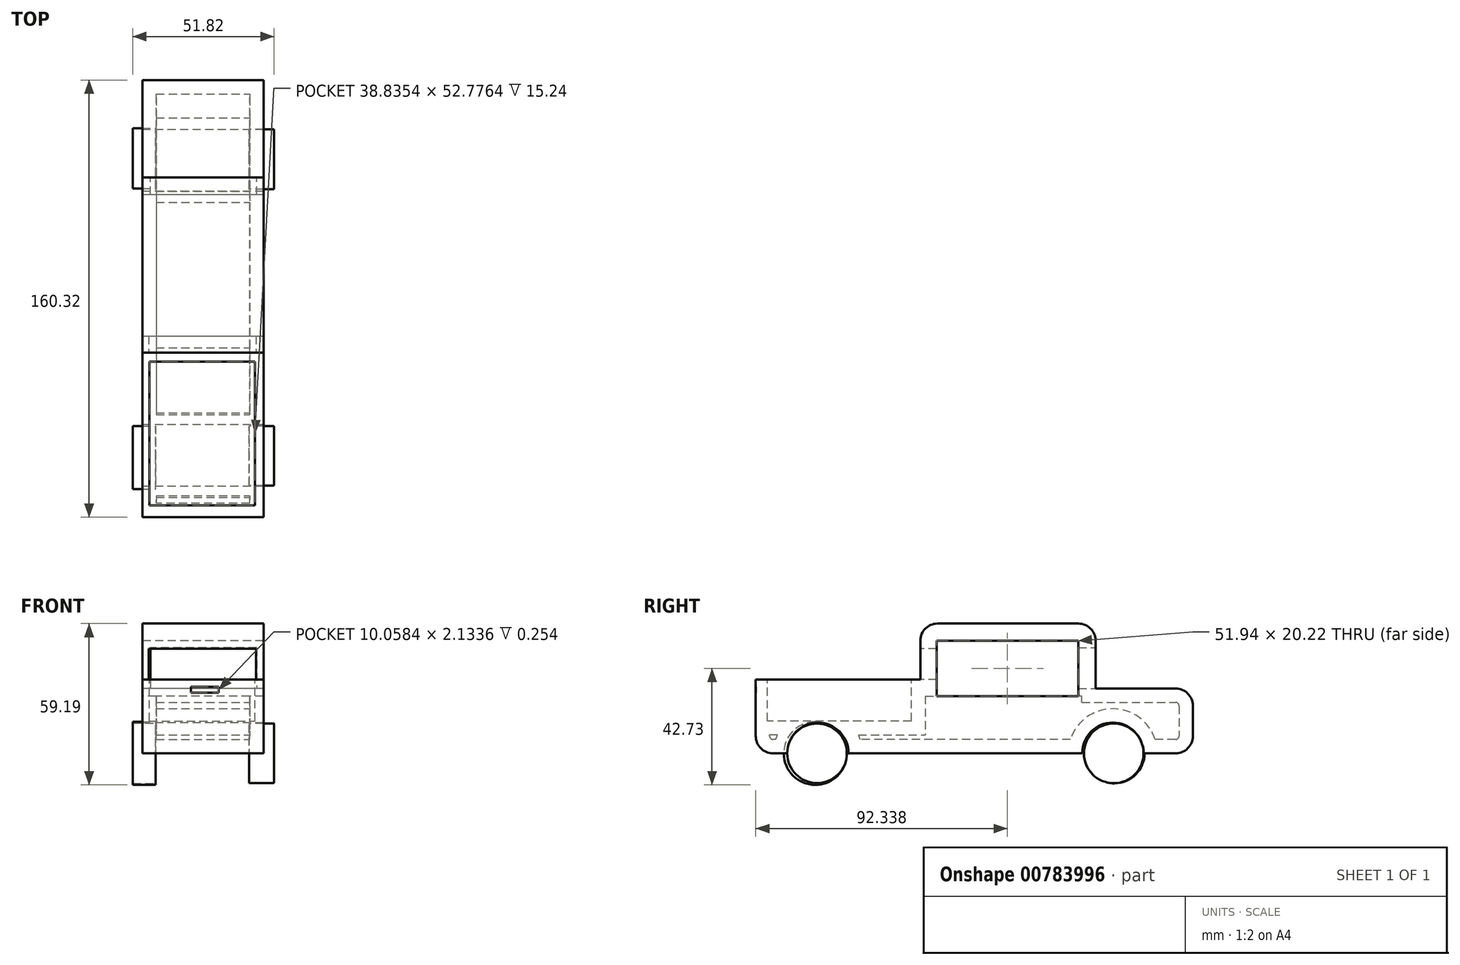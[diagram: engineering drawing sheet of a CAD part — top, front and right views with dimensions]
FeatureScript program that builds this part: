
annotation { "Feature Type Name" : "Feature", "Feature Type Description" : "" }
export const myFeature = defineFeature(function(context is Context, id is Id, definition is map)
    precondition{}
    {
        {
            var Q0;
            Q0=qCreatedBy(makeId("Right.planeOp"),FACE);
            var sketch = newSketch(context, id + "F0", { "sketchPlane" : qUnion([Q0])});
            skLineSegment(sketch, "E0.bottom", {"start": v(34.9, 23.77) * mm, "end": v(64.21, 23.77) * mm});
            skLineSegment(sketch, "E0.top", {"start": v(34.9, 0) * mm, "end": v(64.21, 0) * mm});
            skLineSegment(sketch, "E0.left", {"start": v(34.9, 23.77) * mm, "end": v(34.9, 0) * mm});
            skLineSegment(sketch, "E0.right", {"start": v(70.56, 17.42) * mm, "end": v(70.56, 6.35) * mm});
            skLineSegment(sketch, "E1.bottom", {"start": v(34.9, 0) * mm, "end": v(-29.41, 0) * mm});
            skLineSegment(sketch, "E1.top", {"start": v(28.55, 47.6) * mm, "end": v(-23.06, 47.6) * mm});
            skLineSegment(sketch, "E1.left", {"start": v(34.9, 0) * mm, "end": v(34.9, 41.25) * mm});
            skLineSegment(sketch, "E1.right", {"start": v(-29.41, 0) * mm, "end": v(-29.41, 41.25) * mm});
            skLineSegment(sketch, "E2.bottom", {"start": v(-29.41, 0) * mm, "end": v(-83.41, 0) * mm});
            skLineSegment(sketch, "E2.top", {"start": v(-29.41, 27.13) * mm, "end": v(-89.76, 27.13) * mm});
            skLineSegment(sketch, "E2.left", {"start": v(-29.41, 0) * mm, "end": v(-29.41, 27.13) * mm});
            skLineSegment(sketch, "E2.right", {"start": v(-89.76, 6.35) * mm, "end": v(-89.76, 27.13) * mm});
            skPoint(sketch, "E3.visualSharp", {"position": v(-29.41, 47.6) * mm});
            skArc(sketch, "E3.filletArc", {"start": v(-23.06, 47.6) * mm, "mid": v(-27.55, 45.74) * mm, "end": v(-29.41, 41.25) * mm});
            skPoint(sketch, "E4.visualSharp", {"position": v(-89.76, 0) * mm});
            skArc(sketch, "E4.filletArc", {"start": v(-89.76, 6.35) * mm, "mid": v(-87.9, 1.86) * mm, "end": v(-83.41, 0) * mm});
            skPoint(sketch, "E5.visualSharp", {"position": v(70.56, 0) * mm});
            skArc(sketch, "E5.filletArc", {"start": v(64.21, 0) * mm, "mid": v(68.7, 1.86) * mm, "end": v(70.56, 6.35) * mm});
            skPoint(sketch, "E6.visualSharp", {"position": v(70.56, 23.77) * mm});
            skArc(sketch, "E6.filletArc", {"start": v(70.56, 17.42) * mm, "mid": v(68.7, 21.91) * mm, "end": v(64.21, 23.77) * mm});
            skPoint(sketch, "E7.visualSharp", {"position": v(34.9, 47.6) * mm});
            skArc(sketch, "E7.filletArc", {"start": v(34.9, 41.25) * mm, "mid": v(33.04, 45.74) * mm, "end": v(28.55, 47.6) * mm});
            skSolve(sketch);
        }
        {
            var Q0;
            {var subQ3=sQuery(id+"F0.wireOp",EDGE,"E1.bottom");Q0=makeQuery(id+"F0.imprint","IMPRINT",FACE,{"disambiguationData":[TD([[makeQuery(id+"F0.imprint","IMPRINT",EDGE,{"derivedFrom":subQ3}),-1.0]])]});}
            var Q1;
            Q1=makeQuery(id+"F0.imprint","IMPRINT",FACE,{"disambiguationData":[TD([[makeQuery(id+"F0.imprint","IMPRINT",EDGE,{"derivedFrom":sQuery(id+"F0.wireOp",EDGE,"E2.bottom")}),-1.0]])]});
            var Q2;
            {var subQ2=sQuery(id+"F0.wireOp",EDGE,"E0.bottom");Q2=makeQuery(id+"F0.imprint","IMPRINT",FACE,{"disambiguationData":[TD([[makeQuery(id+"F0.imprint","IMPRINT",EDGE,{"derivedFrom":subQ2}),-1.0]])]});}
            extrude(context, id + "F1", {"entities" : qUnion([Q0, Q1, Q2]), "depth" : 44.45 * mm, "offsetDistance" : 25.4 * mm});
        }
        {
            var Q0;
            Q0=makeQuery(id+"F1.opExtrude","CAP_FACE",FACE,{"disambiguationData":[OSD([sQuery(id+"F0.wireOp",EDGE,"E0.bottom"),sQuery(id+"F0.wireOp",EDGE,"E0.top"),sQuery(id+"F0.wireOp",EDGE,"E0.right"),sQuery(id+"F0.wireOp",EDGE,"E1.bottom"),sQuery(id+"F0.wireOp",EDGE,"E1.top"),sQuery(id+"F0.wireOp",EDGE,"E1.left"),sQuery(id+"F0.wireOp",EDGE,"E1.right"),sQuery(id+"F0.wireOp",EDGE,"E2.bottom"),sQuery(id+"F0.wireOp",EDGE,"E2.top"),sQuery(id+"F0.wireOp",EDGE,"E2.right"),sQuery(id+"F0.wireOp",EDGE,"E3.filletArc"),sQuery(id+"F0.wireOp",EDGE,"E4.filletArc"),sQuery(id+"F0.wireOp",EDGE,"E5.filletArc"),sQuery(id+"F0.wireOp",EDGE,"E6.filletArc"),sQuery(id+"F0.wireOp",EDGE,"E7.filletArc")])],"isStart":false});
            var sketch = newSketch(context, id + "F2", { "sketchPlane" : qUnion([Q0])});
            skCircle(sketch, "E8", {"center": v(-66.98, 0) * mm, "radius": 11.27 * mm});
            skCircle(sketch, "E9", {"center": v(41.22, 0) * mm, "radius": 11.26 * mm});
            skSolve(sketch);
        }
        {
            var Q0;
            {var subQ0=sQuery(id+"F2.wireOp",EDGE,"E9");var subQ1=makeQuery(id+"F1.opExtrude","CAP_EDGE",EDGE,{"disambiguationData":[OSD([sQuery(id+"F0.wireOp",EDGE,"E0.top"),sQuery(id+"F0.wireOp",EDGE,"E1.bottom"),sQuery(id+"F0.wireOp",EDGE,"E2.bottom")])],"isStart":false});var subQ2=makeQuery(id+"F2.imprint","INTERSECT",VERTEX,{"disambiguationData":[OD(0.0)],"derivedFrom":[subQ1,subQ0]});Q0=makeQuery(id+"F2.imprint","IMPRINT",FACE,{"disambiguationData":[TD([[makeQuery(id+"F2.imprint","IMPRINT",EDGE,{"disambiguationData":[TD([[subQ2,1.0]])],"derivedFrom":subQ0}),1.0]])]});}
            var Q1;
            {var subQ0=sQuery(id+"F2.wireOp",EDGE,"E8");var subQ1=makeQuery(id+"F1.opExtrude","CAP_EDGE",EDGE,{"disambiguationData":[OSD([sQuery(id+"F0.wireOp",EDGE,"E0.top"),sQuery(id+"F0.wireOp",EDGE,"E1.bottom"),sQuery(id+"F0.wireOp",EDGE,"E2.bottom")])],"isStart":false});var subQ2=makeQuery(id+"F2.imprint","INTERSECT",VERTEX,{"disambiguationData":[OD(0.0)],"derivedFrom":[subQ1,subQ0]});Q1=makeQuery(id+"F2.imprint","IMPRINT",FACE,{"disambiguationData":[TD([[makeQuery(id+"F2.imprint","IMPRINT",EDGE,{"disambiguationData":[TD([[subQ2,1.0]])],"derivedFrom":subQ0}),1.0]])]});}
            var Q2;
            {var subQ0=sQuery(id+"F2.wireOp",EDGE,"E9");var subQ1=makeQuery(id+"F1.opExtrude","CAP_EDGE",EDGE,{"disambiguationData":[OSD([sQuery(id+"F0.wireOp",EDGE,"E0.top"),sQuery(id+"F0.wireOp",EDGE,"E1.bottom"),sQuery(id+"F0.wireOp",EDGE,"E2.bottom")])],"isStart":false});var subQ2=makeQuery(id+"F2.imprint","INTERSECT",VERTEX,{"disambiguationData":[OD(0.0)],"derivedFrom":[subQ1,subQ0]});Q2=makeQuery(id+"F2.imprint","IMPRINT",FACE,{"disambiguationData":[TD([[makeQuery(id+"F2.imprint","IMPRINT",EDGE,{"disambiguationData":[TD([[subQ2,-1.0]])],"derivedFrom":subQ0}),1.0]])]});}
            var Q3;
            {var subQ0=sQuery(id+"F2.wireOp",EDGE,"E8");var subQ1=makeQuery(id+"F1.opExtrude","CAP_EDGE",EDGE,{"disambiguationData":[OSD([sQuery(id+"F0.wireOp",EDGE,"E0.top"),sQuery(id+"F0.wireOp",EDGE,"E1.bottom"),sQuery(id+"F0.wireOp",EDGE,"E2.bottom")])],"isStart":false});var subQ2=makeQuery(id+"F2.imprint","INTERSECT",VERTEX,{"disambiguationData":[OD(0.0)],"derivedFrom":[subQ1,subQ0]});Q3=makeQuery(id+"F2.imprint","IMPRINT",FACE,{"disambiguationData":[TD([[makeQuery(id+"F2.imprint","IMPRINT",EDGE,{"disambiguationData":[TD([[subQ2,-1.0]])],"derivedFrom":subQ0}),1.0]])]});}
            extrude(context, id + "F3", {"entities" : qUnion([Q0, Q1, Q2, Q3]), "operationType" : NewBodyOperationType.REMOVE, "oppositeDirection" : true, "depth" : 47 * mm, "offsetDistance" : 25.4 * mm});
        }
        {
            var Q0;
            Q0=makeQuery(id+"F1.opExtrude","SWEPT_FACE",FACE,{"disambiguationData":[OSD([sQuery(id+"F0.wireOp",EDGE,"E2.top")])]});
            var sketch = newSketch(context, id + "F4", { "sketchPlane" : qUnion([Q0])});
            skLineSegment(sketch, "E10.bottom", {"start": v(2.49, -32.67) * mm, "end": v(41.32, -32.67) * mm});
            skLineSegment(sketch, "E10.top", {"start": v(2.49, -85.45) * mm, "end": v(41.32, -85.45) * mm});
            skLineSegment(sketch, "E10.left", {"start": v(2.49, -32.67) * mm, "end": v(2.49, -85.45) * mm});
            skLineSegment(sketch, "E10.right", {"start": v(41.32, -32.67) * mm, "end": v(41.32, -85.45) * mm});
            skSolve(sketch);
        }
        {
            var Q0;
            Q0 = qSketchRegion(id + "F4", true);
            extrude(context, id + "F5", {"entities" : qUnion([Q0]), "operationType" : NewBodyOperationType.REMOVE, "oppositeDirection" : true, "depth" : 15.24 * mm, "offsetDistance" : 25.4 * mm});
        }
        {
            var Q0;
            Q0=qCreatedBy(makeId("Right.planeOp"),FACE);
            var sketch = newSketch(context, id + "F6", { "sketchPlane" : qUnion([Q0])});
            skCircle(sketch, "E11", {"center": v(-67.28, 0) * mm, "radius": 10.93 * mm});
            skCircle(sketch, "E12", {"center": v(41.53, 0) * mm, "radius": 10.94 * mm});
            skSolve(sketch);
        }
        {
            var Q0;
            Q0 = qSketchRegion(id + "F6", true);
            extrude(context, id + "F7", {"entities" : qUnion([Q0]), "depth" : 48.26 * mm, "offsetDistance" : 25.4 * mm, "hasSecondDirection" : true, "secondDirectionOppositeDirection" : false, "secondDirectionDepth" : 39.12 * mm});
        }
        {
            var Q0;
            Q0=qCreatedBy(makeId("Right.planeOp"),FACE);
            var sketch = newSketch(context, id + "F8", { "sketchPlane" : qUnion([Q0])});
            skCircle(sketch, "E13", {"center": v(41.83, 0) * mm, "radius": 11.01 * mm});
            skCircle(sketch, "E14", {"center": v(-67.9, 0) * mm, "radius": 11.59 * mm});
            skSolve(sketch);
        }
        {
            var Q0;
            Q0 = qSketchRegion(id + "F8", true);
            extrude(context, id + "F9", {"entities" : qUnion([Q0]), "oppositeDirection" : true, "depth" : 3.56 * mm, "offsetDistance" : 25.4 * mm, "hasSecondDirection" : true, "secondDirectionOppositeDirection" : false, "secondDirectionDepth" : 4.83 * mm});
        }
        {
            var Q0;
            Q0=makeQuery(id+"F1.opExtrude","SWEPT_FACE",FACE,{"disambiguationData":[OSD([sQuery(id+"F0.wireOp",EDGE,"E2.right")])]});
            var sketch = newSketch(context, id + "F10", { "sketchPlane" : qUnion([Q0])});
            skLineSegment(sketch, "E15.bottom", {"start": v(17.83, 24.38) * mm, "end": v(27.89, 24.38) * mm});
            skLineSegment(sketch, "E15.top", {"start": v(17.83, 22.25) * mm, "end": v(27.89, 22.25) * mm});
            skLineSegment(sketch, "E15.left", {"start": v(17.83, 24.38) * mm, "end": v(17.83, 22.25) * mm});
            skLineSegment(sketch, "E15.right", {"start": v(27.89, 24.38) * mm, "end": v(27.89, 22.25) * mm});
            skSolve(sketch);
        }
        {
            var Q0;
            Q0 = qSketchRegion(id + "F10", true);
            extrude(context, id + "F11", {"entities" : qUnion([Q0]), "operationType" : NewBodyOperationType.REMOVE, "oppositeDirection" : true, "depth" : 0.25 * mm, "offsetDistance" : 25.4 * mm});
        }
        {
            var Q0;
            Q0=makeQuery(id+"F1.opExtrude","CAP_FACE",FACE,{"disambiguationData":[OSD([sQuery(id+"F0.wireOp",EDGE,"E0.bottom"),sQuery(id+"F0.wireOp",EDGE,"E0.top"),sQuery(id+"F0.wireOp",EDGE,"E0.right"),sQuery(id+"F0.wireOp",EDGE,"E1.bottom"),sQuery(id+"F0.wireOp",EDGE,"E1.top"),sQuery(id+"F0.wireOp",EDGE,"E1.left"),sQuery(id+"F0.wireOp",EDGE,"E1.right"),sQuery(id+"F0.wireOp",EDGE,"E2.bottom"),sQuery(id+"F0.wireOp",EDGE,"E2.top"),sQuery(id+"F0.wireOp",EDGE,"E2.right"),sQuery(id+"F0.wireOp",EDGE,"E3.filletArc"),sQuery(id+"F0.wireOp",EDGE,"E4.filletArc"),sQuery(id+"F0.wireOp",EDGE,"E5.filletArc"),sQuery(id+"F0.wireOp",EDGE,"E6.filletArc"),sQuery(id+"F0.wireOp",EDGE,"E7.filletArc")])],"isStart":true});
            var sketch = newSketch(context, id + "F12", { "sketchPlane" : qUnion([Q0])});
            skLineSegment(sketch, "E16.bottom", {"start": v(-28.55, 41.25) * mm, "end": v(23.4, 41.25) * mm});
            skLineSegment(sketch, "E16.top", {"start": v(-28.55, 21.03) * mm, "end": v(23.4, 21.03) * mm});
            skLineSegment(sketch, "E16.left", {"start": v(-28.55, 41.25) * mm, "end": v(-28.55, 21.03) * mm});
            skLineSegment(sketch, "E16.right", {"start": v(23.4, 41.25) * mm, "end": v(23.4, 21.03) * mm});
            skSolve(sketch);
        }
        {
            var Q0;
            Q0 = qSketchRegion(id + "F12", true);
            extrude(context, id + "F13", {"entities" : qUnion([Q0]), "operationType" : NewBodyOperationType.REMOVE, "oppositeDirection" : true, "depth" : 55.12 * mm, "offsetDistance" : 25.4 * mm});
        }
        {
            var Q0;
            Q0=makeQuery(id+"F1.opExtrude","SWEPT_FACE",FACE,{"disambiguationData":[OSD([sQuery(id+"F0.wireOp",EDGE,"E1.right")])]});
            var sketch = newSketch(context, id + "F14", { "sketchPlane" : qUnion([Q0])});
            skLineSegment(sketch, "E17.bottom", {"start": v(2.29, 38.4) * mm, "end": v(41.6, 38.4) * mm});
            skLineSegment(sketch, "E17.top", {"start": v(2.29, 27.13) * mm, "end": v(41.6, 27.13) * mm});
            skLineSegment(sketch, "E17.left", {"start": v(2.29, 38.4) * mm, "end": v(2.29, 27.13) * mm});
            skLineSegment(sketch, "E17.right", {"start": v(41.6, 38.4) * mm, "end": v(41.6, 27.13) * mm});
            skSolve(sketch);
        }
        {
            var Q0;
            Q0 = qSketchRegion(id + "F14", true);
            extrude(context, id + "F15", {"entities" : qUnion([Q0]), "operationType" : NewBodyOperationType.REMOVE, "oppositeDirection" : true, "depth" : 25.4 * mm, "offsetDistance" : 25.4 * mm});
        }
        {
            var Q0;
            Q0=makeQuery(id+"F13.boolean.opBoolean","COPY",FACE,{"derivedFrom":makeQuery(id+"F13.opExtrude","SWEPT_FACE",FACE,{"disambiguationData":[OSD([sQuery(id+"F12.wireOp",EDGE,"E16.top")])]})});
            shell(context, id + "F16", {"entities" : qUnion([Q0]), "thickness" : 5.08 * mm});
        }
        {
            var Q0;
            Q0=makeQuery(id+"F1.opExtrude","SWEPT_FACE",FACE,{"disambiguationData":[OSD([sQuery(id+"F0.wireOp",EDGE,"E1.left")])]});
            var sketch = newSketch(context, id + "F17", { "sketchPlane" : qUnion([Q0])});
            skLineSegment(sketch, "E18.bottom", {"start": v(-41.91, 38.7) * mm, "end": v(-2.9, 38.7) * mm});
            skLineSegment(sketch, "E18.top", {"start": v(-41.91, 23.77) * mm, "end": v(-2.9, 23.77) * mm});
            skLineSegment(sketch, "E18.left", {"start": v(-41.91, 38.7) * mm, "end": v(-41.91, 23.77) * mm});
            skLineSegment(sketch, "E18.right", {"start": v(-2.9, 38.7) * mm, "end": v(-2.9, 23.77) * mm});
            skSolve(sketch);
        }
        {
            var Q0;
            Q0 = qSketchRegion(id + "F17", true);
            extrude(context, id + "F18", {"entities" : qUnion([Q0]), "operationType" : NewBodyOperationType.REMOVE, "oppositeDirection" : true, "depth" : 25.4 * mm, "offsetDistance" : 25.4 * mm});
        }
    });
